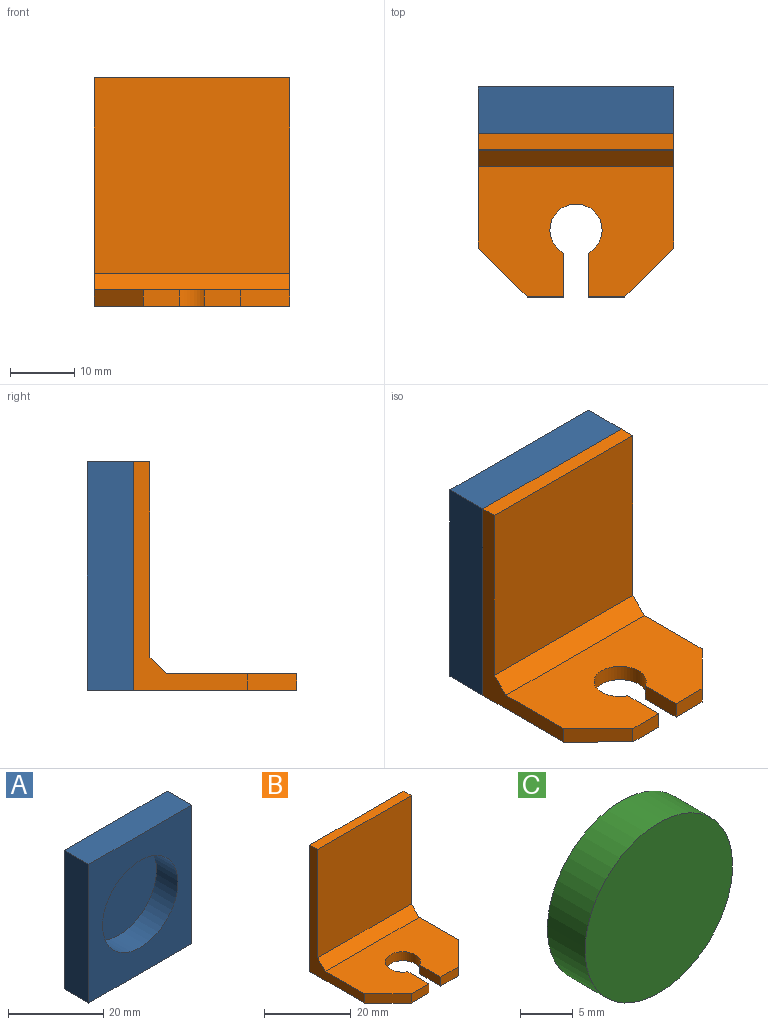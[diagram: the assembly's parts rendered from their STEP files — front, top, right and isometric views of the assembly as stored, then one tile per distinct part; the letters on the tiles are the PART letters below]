
ASSEMBLY  parts=3 mates=2
PART A: 8 faces, bbox 30.5x7.2x35.6 mm
  f0: plane 30.48x7.24mm, normal (0,0,1), area 220.6mm2, adj f1,f3,f4,f5
  f1: plane 35.56x7.24mm, normal (-1,0,0), area 257.4mm2, adj f0,f2,f4,f5
  f2: plane 30.48x7.24mm, normal (0,0,-1), area 220.6mm2, adj f1,f3,f4,f5
  f3: plane 35.56x7.24mm, normal (1,0,0), area 257.4mm2, adj f0,f2,f4,f5
  f4: plane 35.56x30.48mm, normal (0,-1,0), area 691.5mm2, adj f0,f1,f2,f3,f6
  f5: plane 35.56x30.48mm, normal (0,1,0), area 1083.9mm2, adj f0,f1,f2,f3
  f6: cylinder r=11.18mm len=22.35mm, axis (0,-1,0), area 445.9mm2, adj f4,f7
  f7: plane 22.35x22.35mm, normal (0,-1,0), area 392.4mm2, adj f6
PART B: 15 faces, bbox 30.5x25.4x35.6 mm
  f0: plane 5.72x2.54mm, normal (0,-1,0), area 14.5mm2, adj f1,f6,f9,f13
  f1: plane 30.48x20.32mm, normal (0,0,1), area 484.6mm2, adj f0,f3,f5,f8,f9,f10,f11,f12
  f2: plane 30.48x30.48mm, normal (0,-1,0), area 929mm2, adj f3,f4,f5,f14
  f3: plane 35.56x17.78mm, normal (1,0,0), area 132.3mm2, adj f1,f2,f4,f6,f7,f12,f14
  f4: plane 30.48x2.54mm, normal (0,0,1), area 77.4mm2, adj f2,f3,f5,f7
  f5: plane 35.56x17.78mm, normal (-1,0,0), area 132.3mm2, adj f1,f2,f4,f6,f7,f13,f14
  f6: plane 30.48x25.4mm, normal (0,0,-1), area 639.5mm2, adj f0,f3,f5,f7,f8,f9,f10,f11
  f7: plane 35.56x30.48mm, normal (0,1,0), area 1083.9mm2, adj f3,f4,f5,f6
  f8: plane 5.72x2.54mm, normal (0,-1,0), area 14.5mm2, adj f1,f6,f10,f12
  f9: plane 6.82x2.54mm, normal (1,0,0), area 17.3mm2, adj f0,f1,f6,f11
  f10: plane 6.82x2.54mm, normal (-1,0,0), area 17.3mm2, adj f1,f6,f8,f11
  f11: cylinder r=4.06mm len=8.13mm, axis (0,0,1), area 54.8mm2, adj f1,f6,f9,f10
  f12: plane 7.62x7.62mm, normal (0.71,-0.71,0), area 27.4mm2, adj f1,f3,f6,f8
  f13: plane 7.62x7.62mm, normal (-0.71,-0.71,0), area 27.4mm2, adj f0,f1,f5,f6
  f14: plane 30.48x2.54mm, normal (0,-0.71,0.71), area 109.5mm2, adj f1,f2,f3,f5
PART C: 3 faces, bbox 19.8x5.1x19.8 mm
  f0: cylinder r=9.91mm len=19.81mm, axis (0,1,0), area 316.2mm2, adj f1,f2
  f1: plane 19.81x19.81mm, normal (0,-1,0), area 308.3mm2, adj f0
  f2: plane 19.81x19.81mm, normal (0,1,0), area 308.3mm2, adj f0
PLACE A t=(14.9,-62,13.58)mm
PLACE B t=(-33.11,-69.24,-71.85)mm
PLACE C t=(-33.11,-62.89,-22.94)mm
MATE fastened C.f0 <-> A.f6  axis (0,1,0) through (-33.11,-62.89,-22.94)mm
MATE fastened B.f7 <-> A.f4  axis (0,1,0) through (-48.35,-69.24,-5.16)mm
